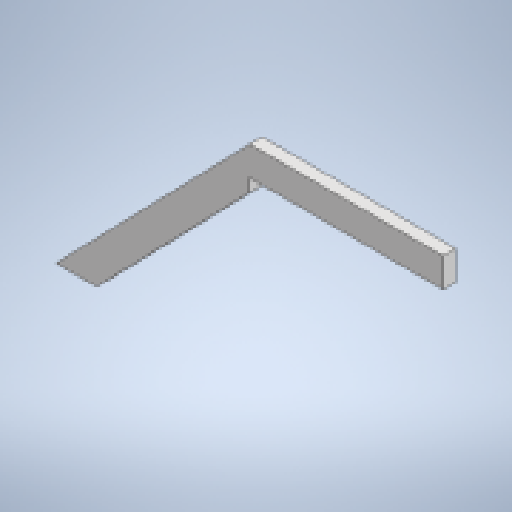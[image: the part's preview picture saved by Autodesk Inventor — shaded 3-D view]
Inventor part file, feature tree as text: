
AUTODESK INVENTOR PART (.ipt)
format: ipt  version: 2025.1 (Build 291241020, 241B)  size: 137,728 bytes
history: native  units: in
note: dims shown in document units (in); Inventor stores cm internally (conversion verified against a paired STEP export)
features: other x5, reference x3, extrude x1, sketch x1
ambient origin geometry x8: Origin, YZ Plane, XZ Plane, XY Plane, X Axis, Y Axis, Z Axis, Center Point
bodies: Solid1 (feature_tree)
feature tree (10):
  extrude  "Extrusion1"  Depth=3.5in
  sketch  "Sketch1"  dims[d0=3.5in d1=3.5in d2=1.5in d3=0.0in]
  reference  "Reference1"
  reference  "Reference2"
  reference  "Reference3"
  other  "<userpath>\Documents\Tburn24\F_Legs2\F_Legs2.iam"
  other  "F_Legs2.iam"
  other  "8'x2x4:4"
  other  "back_side:1"
  other  "side-side:2"
